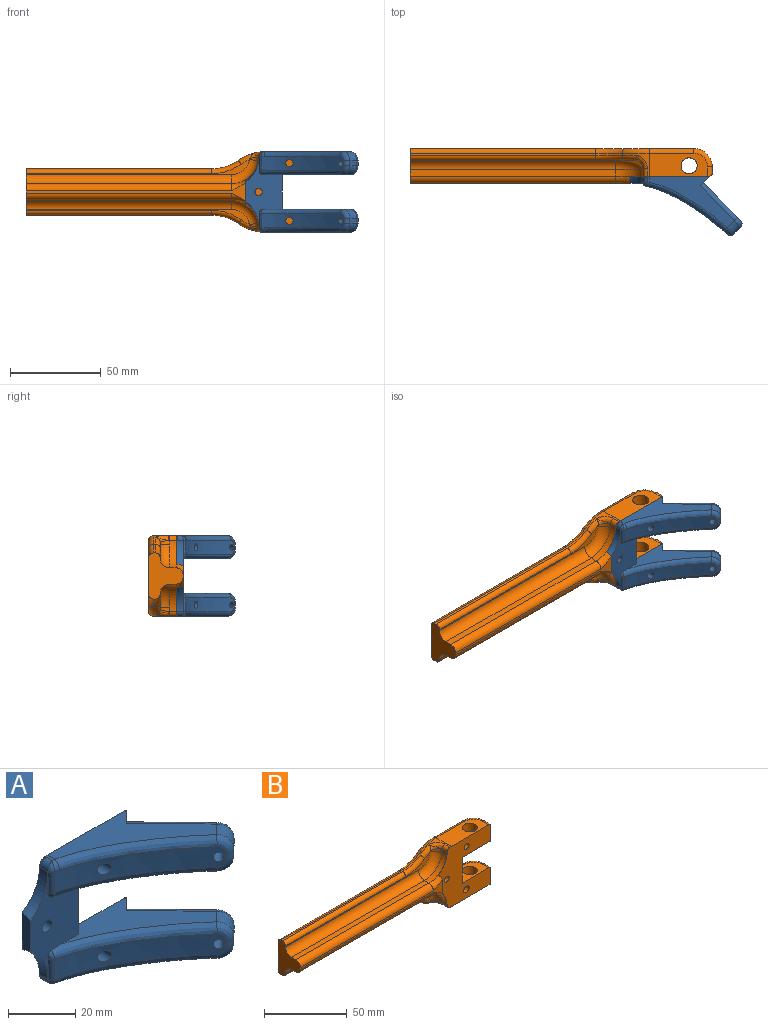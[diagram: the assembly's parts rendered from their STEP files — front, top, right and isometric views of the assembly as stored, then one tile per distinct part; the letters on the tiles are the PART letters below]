
ASSEMBLY  parts=2 mates=1
PART A: 69 faces, bbox 70.2x36.3x66.1 mm
  f0: plane 46.83x28.1mm, normal (0,0,-1), area 409.1mm2, adj f5,f13,f21,f23,f39,f48,f65
  f1: extruded ~45.27x26.58mm, area 375.5mm2, adj f38,f39,f40,f41,f42,f43,f55,f63
  f2: extruded ~45.27x26.58mm, area 375.5mm2, adj f30,f31,f32,f33,f34,f35,f59,f62
  f3: plane 21.09x20.58mm, normal (0.72,0.7,0), area 213.5mm2, adj f13,f44,f45,f46,f47,f48,f63
  f4: plane 3.8x3.71mm, normal (0.7,-0.72,0), area 13.5mm2, adj f18,f21,f41,f46
  f5: cylinder r=25.4mm len=2.99mm, axis (0,-1,0), area 2.9mm2, adj f0,f36,f37,f38,f65
  f6: plane 38.7x20.18mm, normal (0,-1,0), area 372.8mm2, adj f7,f9,f10,f15,f16,f26,f27,f35
  f7: plane 44.79x28.1mm, normal (0,0,-1), area 377.1mm2, adj f6,f10,f14,f19,f24,f35,f53,f65
  f8: plane 46.83x28.1mm, normal (0,0,1), area 409.1mm2, adj f14,f17,f20,f22,f31,f49,f65
  f9: plane 44.79x28.1mm, normal (0,0,1), area 377.1mm2, adj f6,f10,f13,f18,f25,f43,f44,f65
  f10: plane 19.05x3.52mm, normal (1,0,0), area 67mm2, adj f6,f7,f9,f65
  f11: plane 21.09x20.58mm, normal (0.72,0.7,0), area 213.5mm2, adj f14,f49,f50,f51,f52,f53,f62
  f12: plane 3.8x3.71mm, normal (0.7,-0.72,0), area 13.5mm2, adj f19,f20,f33,f51
  f13: plane 12.72x5.07mm, normal (0.71,-0.71,0), area 61.1mm2, adj f0,f3,f9,f23,f25,f44,f48,f65
  f14: plane 12.72x5.07mm, normal (0.71,-0.71,0), area 61.1mm2, adj f7,f8,f11,f22,f24,f49,f53,f65
  f15: plane 8x3.13mm, normal (-1,0,0), area 1.1mm2, adj f6,f26,f29,f58,f59,f60
  f16: plane 8x3.13mm, normal (-1,0,0), area 1.1mm2, adj f6,f27,f37,f54,f55,f56
  f17: cylinder r=25.4mm len=2.99mm, axis (0,1,0), area 2.9mm2, adj f8,f28,f29,f30,f65
  f18: cylinder r=5.08mm len=7.44mm, axis (0.72,0.7,0), area 42.9mm2, adj f4,f9,f42,f45
  f19: cylinder r=5.08mm len=7.44mm, axis (-0.72,-0.7,0), area 42.9mm2, adj f7,f12,f34,f52
  f20: cylinder r=5.08mm len=7.44mm, axis (0.72,0.7,0), area 42.9mm2, adj f8,f12,f32,f50
  f21: cylinder r=5.08mm len=7.44mm, axis (-0.72,-0.7,0), area 42.9mm2, adj f0,f4,f40,f47
  f22: cylinder r=2.54mm len=0.98mm, axis (0,1,0), area 0.5mm2, adj f8,f14,f65
  f23: cylinder r=2.54mm len=0.98mm, axis (0,-1,0), area 0.5mm2, adj f0,f13,f65
  f24: cylinder r=2.54mm len=0.98mm, axis (0,1,0), area 0.5mm2, adj f7,f14,f65
  f25: cylinder r=2.54mm len=0.98mm, axis (0,-1,0), area 0.5mm2, adj f9,f13,f65
  f26: torus R=19.05mm, axis (1,0,0), area 55.9mm2, adj f6,f15,f28,f64,f65
  f27: torus R=19.05mm, axis (1,0,0), area 55.9mm2, adj f6,f16,f36,f64,f65
  f28: bspline ~6.09x2.58mm, area 1.8mm2, adj f17,f26,f29,f65
  f29: cylinder r=2.54mm len=3.13mm, axis (0,1,0), area 10.6mm2, adj f15,f17,f28,f61
  f30: bspline ~6.13x3.75mm, area 5.9mm2, adj f2,f17,f31,f60,f61
  f31: bspline ~50.66x29.85mm, area 196.9mm2, adj f2,f8,f30,f32
  f32: bspline ~6.18x6.06mm, area 25.4mm2, adj f2,f20,f31,f33
  f33: cylinder r=2.54mm len=3.53mm, axis (0,0,-1), area 9.9mm2, adj f2,f12,f32,f34
  f34: bspline ~6.22x6.18mm, area 25.4mm2, adj f2,f19,f33,f35
  f35: bspline ~49.5x29.64mm, area 202.1mm2, adj f2,f6,f7,f34,f58
  f36: bspline ~6.09x2.58mm, area 1.8mm2, adj f5,f27,f37,f65
  f37: cylinder r=2.54mm len=3.13mm, axis (0,-1,0), area 10.6mm2, adj f5,f16,f36,f57
  f38: bspline ~6.13x3.75mm, area 5.9mm2, adj f1,f5,f39,f56,f57
  f39: bspline ~50.66x29.85mm, area 196.9mm2, adj f0,f1,f38,f40
  f40: bspline ~6.22x6.18mm, area 25.4mm2, adj f1,f21,f39,f41
  f41: cylinder r=2.54mm len=3.53mm, axis (0,0,-1), area 9.9mm2, adj f1,f4,f40,f42
  f42: bspline ~6.22x6.18mm, area 25.4mm2, adj f1,f18,f41,f43
  f43: bspline ~49.5x29.64mm, area 202.1mm2, adj f1,f6,f9,f42,f54
  f44: cylinder r=2.54mm len=21.04mm, axis (-0.7,0.72,0), area 107.2mm2, adj f3,f9,f13,f45
  f45: torus R=2.54mm, axis (-0.72,-0.7,0), area 26mm2, adj f3,f18,f44,f46
  f46: cylinder r=2.54mm len=3.59mm, axis (0,0,1), area 10.1mm2, adj f3,f4,f45,f47
  f47: torus R=2.54mm, axis (-0.72,-0.7,0), area 26mm2, adj f3,f21,f46,f48
  f48: cylinder r=2.54mm len=21.04mm, axis (0.7,-0.72,0), area 107.2mm2, adj f0,f3,f13,f47
  f49: cylinder r=2.54mm len=21.04mm, axis (-0.7,0.72,0), area 107.2mm2, adj f8,f11,f14,f50
  f50: torus R=2.54mm, axis (-0.72,-0.7,0), area 26mm2, adj f11,f20,f49,f51
  f51: cylinder r=2.54mm len=3.59mm, axis (0,0,1), area 10.1mm2, adj f11,f12,f50,f52
  f52: torus R=2.54mm, axis (-0.72,-0.7,0), area 26mm2, adj f11,f19,f51,f53
  f53: cylinder r=2.54mm len=21.04mm, axis (-0.7,0.72,0), area 107.2mm2, adj f7,f11,f14,f52
  f54: bspline ~2.81x2.28mm, area 4.3mm2, adj f6,f16,f43,f55
  f55: cylinder r=1.52mm len=7.56mm, axis (0,0,-1), area 15.7mm2, adj f1,f16,f54,f56
  f56: bspline ~1.5x1.22mm, area 0.2mm2, adj f16,f38,f55,f57
  f57: bspline ~3.13x2.44mm, area 3.5mm2, adj f37,f38,f56
  f58: bspline ~2.81x2.28mm, area 4.3mm2, adj f6,f15,f35,f59
  f59: cylinder r=1.52mm len=7.56mm, axis (0,0,-1), area 15.7mm2, adj f2,f15,f58,f60
  f60: bspline ~1.5x1.22mm, area 0.2mm2, adj f15,f30,f59,f61
  f61: bspline ~2.65x2.44mm, area 3.5mm2, adj f29,f30,f60
  f62: cylinder r=1.63mm len=9.85mm, axis (0.72,0.7,0), area 108.4mm2, adj f2,f11
  f63: cylinder r=1.63mm len=9.85mm, axis (0.72,0.7,0), area 108.4mm2, adj f1,f3
  f64: plane 13.23x3.52mm, normal (-1,0,0), area 43.3mm2, adj f6,f26,f27,f65
  f65: plane 44.61x44.09mm, normal (0,1,0), area 1282.1mm2, adj f0,f5,f7,f8,f9,f10,f13,f14
  f66: cylinder r=2.03mm len=10.62mm, axis (0,1,0), area 135.6mm2, adj f2,f65
  f67: cylinder r=2.03mm len=10.62mm, axis (0,1,0), area 135.6mm2, adj f1,f65
  f68: cylinder r=2.03mm len=4.06mm, axis (0,1,0), area 44.9mm2, adj f6,f65
PART B: 81 faces, bbox 168.3x37.4x52.9 mm
  f0: cylinder r=25.4mm len=14.81mm, axis (0,-1,0), area 43.5mm2, adj f16,f22,f31,f38,f48,f69,f70,f71
  f1: plane 121.24x10.52mm, normal (0,-1,0), area 187.5mm2, adj f13,f14,f33,f34,f72,f73
  f2: plane 22.86x12.99mm, normal (0,0,-1), area 222.5mm2, adj f5,f11,f26,f51,f52,f74
  f3: plane 32.12x12.99mm, normal (0,0,1), area 342.9mm2, adj f8,f9,f26,f44,f45,f74
  f4: plane 22.86x12.99mm, normal (0,0,1), area 222.5mm2, adj f5,f12,f25,f54,f55,f74
  f5: plane 19.05x12.99mm, normal (1,0,0), area 247.5mm2, adj f2,f4,f53,f74
  f6: plane 13.02x2.28mm, normal (0.71,-0.71,0), area 24.4mm2, adj f10,f12,f24,f74
  f7: plane 13.02x2.28mm, normal (0.71,-0.71,0), area 24.4mm2, adj f9,f11,f23,f74
  f8: cylinder r=25.4mm len=14.81mm, axis (0,1,0), area 43.5mm2, adj f3,f15,f32,f35,f43,f66,f67,f68
  f9: cylinder r=2.54mm len=5.37mm, axis (0,1,0), area 19.1mm2, adj f3,f7,f23,f45,f74
  f10: cylinder r=2.54mm len=5.37mm, axis (0,-1,0), area 19.1mm2, adj f6,f22,f24,f50,f74
  f11: cylinder r=2.54mm len=5.37mm, axis (0,1,0), area 19.1mm2, adj f2,f7,f23,f51,f74
  f12: cylinder r=2.54mm len=5.37mm, axis (0,-1,0), area 19.1mm2, adj f4,f6,f24,f55,f74
  f13: torus R=19.05mm, axis (1,0,0), area 44.8mm2, adj f1,f15,f34,f56,f73,f74
  f14: torus R=19.05mm, axis (1,0,0), area 44.8mm2, adj f1,f16,f33,f57,f73,f74
  f15: bspline ~3.92x2.55mm, area 1.1mm2, adj f8,f13,f68,f74
  f16: bspline ~3.92x2.55mm, area 1.1mm2, adj f0,f14,f71,f74
  f17: plane 156.56x39.37mm, normal (0,1,0), area 3490.9mm2, adj f27,f28,f41,f42,f43,f44,f46,f47
  f18: plane 123.39x8.46mm, normal (0,-1,0), area 115.8mm2, adj f38,f39,f40,f64,f65,f72
  f19: plane 113.38x3.81mm, normal (0,0,-1), area 432mm2, adj f33,f57,f65,f72
  f20: plane 123.39x8.46mm, normal (0,-1,0), area 115.8mm2, adj f35,f36,f37,f60,f61,f72
  f21: plane 113.38x3.81mm, normal (0,0,1), area 432mm2, adj f34,f56,f61,f72
  f22: plane 32.12x12.99mm, normal (0,0,-1), area 342.9mm2, adj f0,f10,f25,f49,f50,f74
  f23: plane 7.62x3.81mm, normal (1,0,0), area 29mm2, adj f7,f9,f11,f28
  f24: plane 7.62x3.81mm, normal (1,0,0), area 29mm2, adj f6,f10,f12,f27
  f25: cylinder r=4.45mm len=12.7mm, axis (0,0,1), area 354.7mm2, adj f4,f22
  f26: cylinder r=4.45mm len=12.7mm, axis (0,0,1), area 354.7mm2, adj f2,f3
  f27: cylinder r=10.16mm len=10.16mm, axis (0,0,1), area 121.6mm2, adj f17,f24,f50,f55
  f28: cylinder r=10.16mm len=10.16mm, axis (0,0,1), area 121.6mm2, adj f17,f23,f45,f51
  f29: plane 102.44x1.27mm, normal (0,0,1), area 130.1mm2, adj f32,f37,f41,f72
  f30: plane 102.44x1.27mm, normal (0,0,-1), area 130.1mm2, adj f31,f40,f46,f72
  f31: cylinder r=25.4mm len=14.81mm, axis (0,-1,0), area 20.1mm2, adj f0,f30,f39,f47
  f32: cylinder r=25.4mm len=14.81mm, axis (0,1,0), area 20.1mm2, adj f8,f29,f36,f42
  f33: cylinder r=3.81mm len=113.38mm, axis (-1,0,0), area 678.5mm2, adj f1,f14,f19,f72
  f34: cylinder r=3.81mm len=113.38mm, axis (1,0,0), area 678.5mm2, adj f1,f13,f21,f72
  f35: torus R=22.86mm, axis (0,-1,0), area 30.1mm2, adj f8,f20,f36,f58,f59
  f36: torus R=27.94mm, axis (0,-1,0), area 65.4mm2, adj f20,f32,f35,f37
  f37: cylinder r=2.54mm len=102.44mm, axis (-1,0,0), area 408.7mm2, adj f20,f29,f36,f72
  f38: torus R=22.86mm, axis (0,1,0), area 30.1mm2, adj f0,f18,f39,f62,f63
  f39: torus R=27.94mm, axis (0,1,0), area 65.4mm2, adj f18,f31,f38,f40
  f40: cylinder r=2.54mm len=102.44mm, axis (1,0,0), area 408.7mm2, adj f18,f30,f39,f72
  f41: cylinder r=2.54mm len=102.44mm, axis (-1,0,0), area 408.7mm2, adj f17,f29,f42,f72
  f42: torus R=27.94mm, axis (0,-1,0), area 65.4mm2, adj f17,f32,f41,f43
  f43: torus R=22.86mm, axis (0,-1,0), area 60.8mm2, adj f8,f17,f42,f44
  f44: cylinder r=2.54mm len=24.5mm, axis (-1,0,0), area 97.8mm2, adj f3,f17,f43,f45
  f45: torus R=7.62mm, axis (0,0,1), area 57.9mm2, adj f3,f9,f28,f44
  f46: cylinder r=2.54mm len=102.44mm, axis (1,0,0), area 408.7mm2, adj f17,f30,f47,f72
  f47: torus R=27.94mm, axis (0,-1,0), area 65.4mm2, adj f17,f31,f46,f48
  f48: torus R=22.86mm, axis (0,-1,0), area 60.8mm2, adj f0,f17,f47,f49
  f49: cylinder r=2.54mm len=24.5mm, axis (1,0,0), area 97.8mm2, adj f17,f22,f48,f50
  f50: torus R=7.62mm, axis (0,0,1), area 57.9mm2, adj f10,f22,f27,f49
  f51: torus R=7.62mm, axis (0,0,-1), area 57.9mm2, adj f2,f11,f28,f52
  f52: cylinder r=2.54mm len=17.78mm, axis (1,0,0), area 65.9mm2, adj f2,f17,f51,f53
  f53: cylinder r=2.54mm len=24.13mm, axis (0,0,1), area 86.1mm2, adj f5,f17,f52,f54
  f54: cylinder r=2.54mm len=17.78mm, axis (-1,0,0), area 65.9mm2, adj f4,f17,f53,f55
  f55: torus R=7.62mm, axis (0,0,-1), area 57.9mm2, adj f4,f12,f27,f54
  f56: cylinder r=15.24mm len=15.24mm, axis (0,1,0), area 91.4mm2, adj f13,f21,f59,f60,f68
  f57: cylinder r=15.24mm len=15.24mm, axis (0,-1,0), area 91.4mm2, adj f14,f19,f63,f64,f71
  f58: bspline ~8.19x8.07mm, area 9.6mm2, adj f35,f59,f66
  f59: bspline ~5.71x5.46mm, area 13mm2, adj f35,f56,f58,f60,f67
  f60: torus R=10.16mm, axis (0,-1,0), area 149.9mm2, adj f20,f56,f59,f61
  f61: cylinder r=5.08mm len=113.38mm, axis (-1,0,0), area 904.7mm2, adj f20,f21,f60,f72
  f62: bspline ~8.19x8.07mm, area 9.6mm2, adj f38,f63,f69
  f63: bspline ~6.19x5.77mm, area 13mm2, adj f38,f57,f62,f64,f70
  f64: torus R=10.16mm, axis (0,1,0), area 149.9mm2, adj f18,f57,f63,f65
  f65: cylinder r=5.08mm len=113.38mm, axis (1,0,0), area 904.7mm2, adj f18,f19,f64,f72
  f66: bspline ~8.09x6.1mm, area 24.7mm2, adj f8,f58,f67
  f67: bspline ~2.54x2.44mm, area 0.2mm2, adj f8,f59,f66,f68
  f68: cylinder r=2.54mm len=3.96mm, axis (0,-1,0), area 15.4mm2, adj f8,f15,f56,f67
  f69: bspline ~8.09x6.1mm, area 24.7mm2, adj f0,f62,f70
  f70: bspline ~3.46x2.6mm, area 0.2mm2, adj f0,f63,f69,f71
  f71: cylinder r=2.54mm len=3.96mm, axis (0,1,0), area 15.4mm2, adj f0,f16,f57,f70
  f72: plane 25.4x19.05mm, normal (-1,0,0), area 273.5mm2, adj f1,f17,f18,f19,f20,f21,f29,f30
  f73: plane 13.23x3.52mm, normal (1,0,0), area 43.3mm2, adj f1,f13,f14,f74
  f74: plane 44.61x44.09mm, normal (0,-1,0), area 1277.8mm2, adj f0,f2,f3,f4,f5,f6,f7,f8
  f75: cylinder r=2.07mm len=12.7mm, axis (0,-1,0), area 165.4mm2, adj f74,f76
  f76: plane 4.15x4.15mm, normal (0,-1,0), area 13.5mm2, adj f75
  f77: cylinder r=2.03mm len=12.7mm, axis (0,-1,0), area 162.1mm2, adj f74,f78
  f78: plane 4.06x4.06mm, normal (0,-1,0), area 13mm2, adj f77
  f79: cylinder r=2.31mm len=12.7mm, axis (0,-1,0), area 184.4mm2, adj f74,f80
  f80: plane 4.62x4.62mm, normal (0,-1,0), area 16.8mm2, adj f79
PLACE A t=(82.79,4.41,8.03)mm
PLACE B t=(82.79,4.41,8.03)mm
MATE planar A.f65 <-> B.f74  axis (0,1,0) through (45.31,-11.12,4.85)mm
